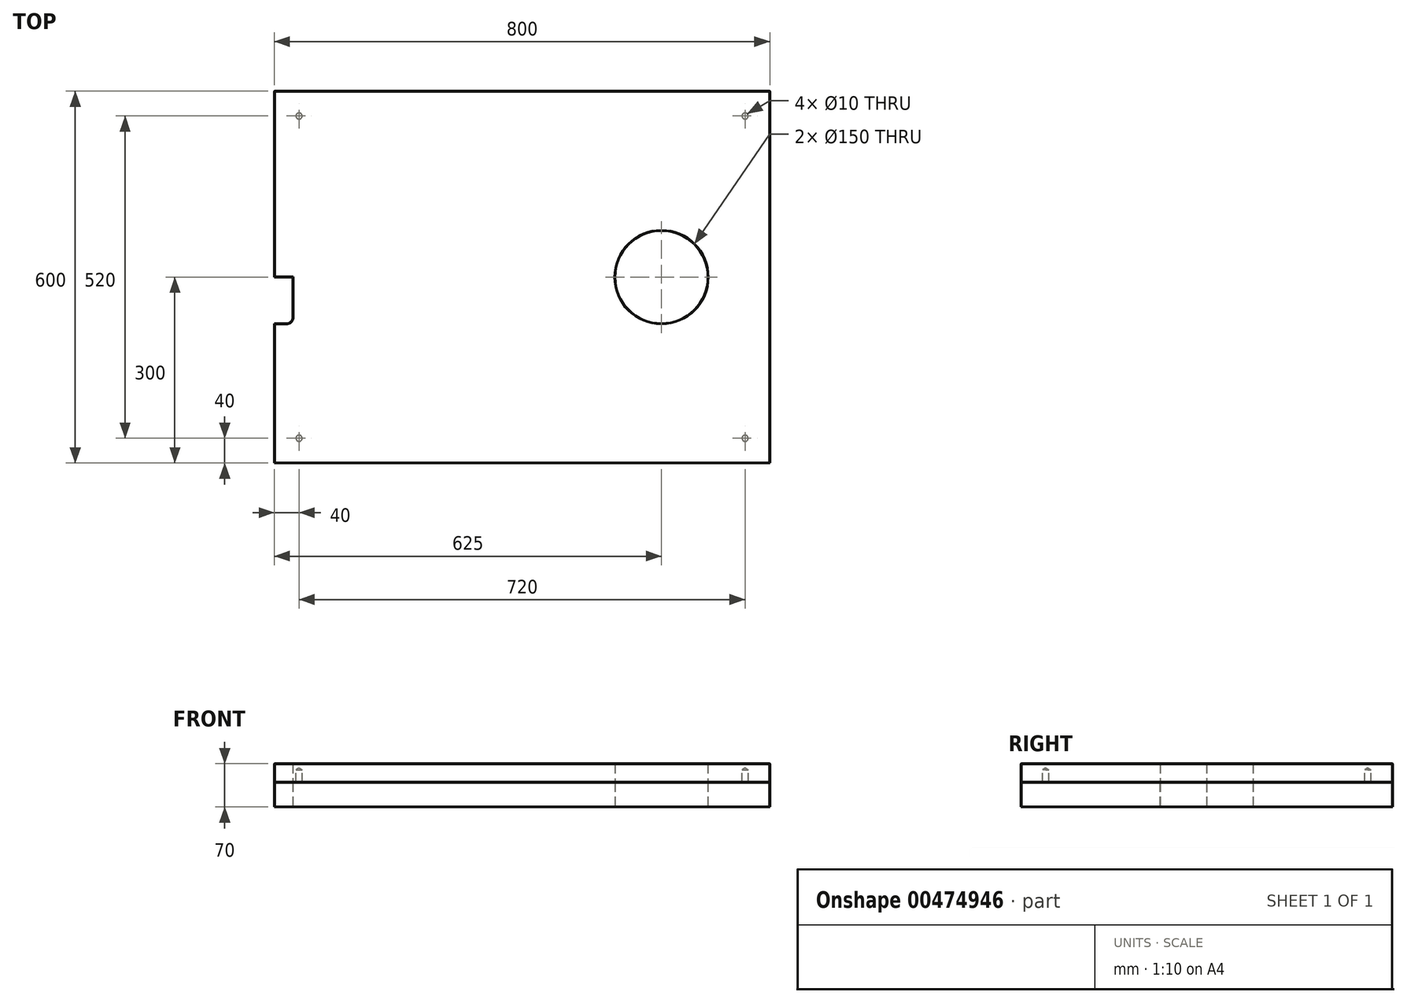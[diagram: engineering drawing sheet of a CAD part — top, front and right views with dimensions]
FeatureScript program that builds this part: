
annotation { "Feature Type Name" : "Feature", "Feature Type Description" : "" }
export const myFeature = defineFeature(function(context is Context, id is Id, definition is map)
    precondition{}
    {
        {
            var Q0;
            Q0=qCreatedBy(makeId("Top.planeOp"),FACE);
            var sketch = newSketch(context, id + "F0", { "sketchPlane" : qUnion([Q0])});
            skLineSegment(sketch, "E0", {"start": v(-450, 0) * mm, "end": v(350, 0) * mm, "construction": true});
            skLineSegment(sketch, "E1.bottom", {"start": v(350, 75) * mm, "end": v(330, 75) * mm});
            skLineSegment(sketch, "E1.top", {"start": v(350, -75) * mm, "end": v(330, -75) * mm});
            skLineSegment(sketch, "E1.left", {"start": v(350, 75) * mm, "end": v(350, -75) * mm});
            skLineSegment(sketch, "E1.right", {"start": v(320, 65) * mm, "end": v(320, -65) * mm});
            skPoint(sketch, "E2.visualSharp", {"position": v(320, -75) * mm});
            skArc(sketch, "E2.filletArc", {"start": v(320, -65) * mm, "mid": v(322.93, -72.07) * mm, "end": v(330, -75) * mm});
            skPoint(sketch, "E3.visualSharp", {"position": v(320, 75) * mm});
            skArc(sketch, "E3.filletArc", {"start": v(330, 75) * mm, "mid": v(322.93, 72.07) * mm, "end": v(320, 65) * mm});
            skLineSegment(sketch, "E4", {"start": v(-50, 300) * mm, "end": v(-50, -300) * mm, "construction": true});
            skLineSegment(sketch, "E5.MirrorCS", {"start": v(-450, 75) * mm, "end": v(-430, 75) * mm});
            skLineSegment(sketch, "E6.MirrorCS", {"start": v(-420, 65) * mm, "end": v(-420, -65) * mm});
            skArc(sketch, "E7.MirrorCS", {"start": v(-420, -65) * mm, "mid": v(-422.93, -72.07) * mm, "end": v(-430, -75) * mm});
            skArc(sketch, "E8.MirrorCS", {"start": v(-430, 75) * mm, "mid": v(-422.93, 72.07) * mm, "end": v(-420, 65) * mm});
            skLineSegment(sketch, "E9.MirrorCS", {"start": v(-450, -75) * mm, "end": v(-430, -75) * mm});
            skPoint(sketch, "E10", {"position": v(-410, 260) * mm});
            skPoint(sketch, "E11", {"position": v(310, 260) * mm});
            skPoint(sketch, "E12", {"position": v(310, -260) * mm});
            skPoint(sketch, "E13", {"position": v(-410, -260) * mm});
            skLineSegment(sketch, "E14", {"start": v(-420, 0) * mm, "end": v(-450, 0) * mm});
            skLineSegment(sketch, "E15.bottom", {"start": v(350, 300) * mm, "end": v(-450, 300) * mm});
            skLineSegment(sketch, "E15.top", {"start": v(350, -300) * mm, "end": v(-450, -300) * mm});
            skLineSegment(sketch, "E15.left", {"start": v(350, 300) * mm, "end": v(350, -300) * mm});
            skLineSegment(sketch, "E15.right", {"start": v(-450, 300) * mm, "end": v(-450, -300) * mm});
            skPoint(sketch, "E15.middle", {"position": v(-50, 0) * mm});
            skPoint(sketch, "E16", {"position": v(175, 0) * mm});
            skCircle(sketch, "E17", {"center": v(175, 0) * mm, "radius": 75 * mm});
            skSolve(sketch);
        }
        {
            var Q0;
            Q0=makeQuery(id+"F0.imprint","IMPRINT",FACE,{"disambiguationData":[TD([[makeQuery(id+"F0.imprint","IMPRINT",EDGE,{"derivedFrom":sQuery(id+"F0.wireOp",EDGE,"9696f999-dd8b-4db2-95aa-c8651f8d9f2f.bottom")}),1.0]])]});
            var Q1;
            {var subQ5=sQuery(id+"F0.wireOp",EDGE,"E1.bottom");Q1=makeQuery(id+"F0.imprint","IMPRINT",FACE,{"disambiguationData":[TD([[makeQuery(id+"F0.imprint","IMPRINT",EDGE,{"derivedFrom":subQ5}),-1.0]])]});}
            var Q2;
            {var subQ1=sQuery(id+"F0.wireOp",EDGE,"E1.bottom");Q2=makeQuery(id+"F0.imprint","IMPRINT",FACE,{"disambiguationData":[TD([[makeQuery(id+"F0.imprint","IMPRINT",EDGE,{"derivedFrom":subQ1}),1.0]])]});}
            var Q3;
            {var subQ2=sQuery(id+"F0.wireOp",EDGE,"E7.MirrorCS");Q3=makeQuery(id+"F0.imprint","IMPRINT",FACE,{"disambiguationData":[TD([[makeQuery(id+"F0.imprint","IMPRINT",EDGE,{"derivedFrom":subQ2}),-1.0]])]});}
            var Q4;
            {var subQ3=sQuery(id+"F0.wireOp",EDGE,"E5.MirrorCS");Q4=makeQuery(id+"F0.imprint","IMPRINT",FACE,{"disambiguationData":[TD([[makeQuery(id+"F0.imprint","IMPRINT",EDGE,{"derivedFrom":subQ3}),-1.0]])]});}
            extrude(context, id + "F1", {"entities" : qUnion([Q0, Q1, Q2, Q3, Q4]), "depth" : 40 * mm, "offsetDistance" : 25 * mm});
        }
        {
            var Q0;
            Q0=makeQuery(id+"F1.opExtrude","CAP_FACE",FACE,{"disambiguationData":[OSD([sQuery(id+"F0.wireOp",EDGE,"E15.bottom"),sQuery(id+"F0.wireOp",EDGE,"E15.top"),sQuery(id+"F0.wireOp",EDGE,"E15.left"),sQuery(id+"F0.wireOp",EDGE,"E15.right")])],"isStart":false});
            var sketch = newSketch(context, id + "F2", { "sketchPlane" : qUnion([Q0])});
            skLineSegment(sketch, "E18.0", {"start": v(350, -75) * mm, "end": v(330, -75) * mm});
            skArc(sketch, "E19.0", {"start": v(320, -65) * mm, "mid": v(322.93, -72.07) * mm, "end": v(330, -75) * mm});
            skLineSegment(sketch, "E20.0", {"start": v(320, 65) * mm, "end": v(320, -65) * mm});
            skArc(sketch, "E21.0", {"start": v(330, 75) * mm, "mid": v(322.93, 72.07) * mm, "end": v(320, 65) * mm});
            skLineSegment(sketch, "E22.0", {"start": v(350, 75) * mm, "end": v(330, 75) * mm});
            skLineSegment(sketch, "E23.0", {"start": v(-450, -75) * mm, "end": v(-430, -75) * mm});
            skArc(sketch, "E24.0", {"start": v(-420, -65) * mm, "mid": v(-422.93, -72.07) * mm, "end": v(-430, -75) * mm});
            skLineSegment(sketch, "E25.0", {"start": v(-420, 65) * mm, "end": v(-420, -65) * mm});
            skArc(sketch, "E26.0", {"start": v(-430, 75) * mm, "mid": v(-422.93, 72.07) * mm, "end": v(-420, 65) * mm});
            skLineSegment(sketch, "E27.0", {"start": v(-450, 75) * mm, "end": v(-430, 75) * mm});
            skSolve(sketch);
        }
        {
            var Q0;
            Q0=makeQuery(id+"F1.opExtrude","CAP_FACE",FACE,{"disambiguationData":[OSD([sQuery(id+"F0.wireOp",EDGE,"E1.bottom"),sQuery(id+"F0.wireOp",EDGE,"E1.top"),sQuery(id+"F0.wireOp",EDGE,"E1.right"),sQuery(id+"F0.wireOp",EDGE,"E2.filletArc"),sQuery(id+"F0.wireOp",EDGE,"E3.filletArc"),sQuery(id+"F0.wireOp",EDGE,"E5.MirrorCS"),sQuery(id+"F0.wireOp",EDGE,"E6.MirrorCS"),sQuery(id+"F0.wireOp",EDGE,"E7.MirrorCS"),sQuery(id+"F0.wireOp",EDGE,"E8.MirrorCS"),sQuery(id+"F0.wireOp",EDGE,"E9.MirrorCS"),sQuery(id+"F0.wireOp",EDGE,"E15.bottom"),sQuery(id+"F0.wireOp",EDGE,"E15.top"),sQuery(id+"F0.wireOp",EDGE,"E15.left"),sQuery(id+"F0.wireOp",EDGE,"E15.right")])],"isStart":false});
            var sketch = newSketch(context, id + "F3", { "sketchPlane" : qUnion([Q0])});
            skLineSegment(sketch, "E28.bottom", {"start": v(-450, 300) * mm, "end": v(350, 300) * mm});
            skLineSegment(sketch, "E28.top", {"start": v(-450, -300) * mm, "end": v(350, -300) * mm});
            skLineSegment(sketch, "E28.left", {"start": v(-450, 300) * mm, "end": v(-450, -300) * mm});
            skLineSegment(sketch, "E28.right", {"start": v(350, 300) * mm, "end": v(350, -300) * mm});
            skLineSegment(sketch, "E29.0", {"start": v(-410, 260) * mm, "end": v(310, 260) * mm});
            skLineSegment(sketch, "E29.1", {"start": v(-410, 260) * mm, "end": v(-410, -260) * mm});
            skLineSegment(sketch, "E29.2", {"start": v(-410, -260) * mm, "end": v(310, -260) * mm});
            skLineSegment(sketch, "E29.3", {"start": v(310, 260) * mm, "end": v(310, -260) * mm});
            skSolve(sketch);
        }
        {
            var Q0;
            {var subQ1=makeQuery(id+"F1.opExtrude","CAP_EDGE",EDGE,{"disambiguationData":[OSD([sQuery(id+"F0.wireOp",EDGE,"E1.bottom")])],"isStart":false});Q0=makeQuery(id+"F3.imprint","IMPRINT",FACE,{"disambiguationData":[TD([[makeQuery(id+"F3.imprint","IMPRINT",EDGE,{"derivedFrom":subQ1}),1.0]])]});}
            var Q1;
            {var subQ4=sQuery(id+"F3.wireOp",EDGE,"E28.bottom");Q1=makeQuery(id+"F3.imprint","IMPRINT",FACE,{"disambiguationData":[TD([[makeQuery(id+"F3.imprint","IMPRINT",EDGE,{"derivedFrom":subQ4}),1.0]])]});}
            var Q2;
            {var subQ0=makeQuery(id+"F1.opExtrude","CAP_EDGE",EDGE,{"disambiguationData":[OSD([sQuery(id+"F0.wireOp",EDGE,"E5.MirrorCS")])],"isStart":false});Q2=makeQuery(id+"F3.imprint","IMPRINT",FACE,{"disambiguationData":[TD([[makeQuery(id+"F3.imprint","IMPRINT",EDGE,{"derivedFrom":subQ0}),-1.0]])]});}
            var Q3;
            Q3=makeQuery(id+"F3.imprint","IMPRINT",FACE,{"disambiguationData":[TD([[makeQuery(id+"F3.imprint","IMPRINT",EDGE,{"derivedFrom":sQuery(id+"F3.wireOp",EDGE,"E29.0")}),-1.0]])]});
            var Q4;
            {var subQ4=sQuery(id+"F3.wireOp",EDGE,"E28.bottom");Q4=makeQuery(id+"F3.imprint","IMPRINT",FACE,{"disambiguationData":[TD([[makeQuery(id+"F3.imprint","IMPRINT",EDGE,{"derivedFrom":subQ4}),1.0]])]});}
            var Q5;
            Q5=makeQuery(id+"F3.imprint","IMPRINT",FACE,{"disambiguationData":[TD([[makeQuery(id+"F3.imprint","IMPRINT",EDGE,{"derivedFrom":sQuery(id+"F3.wireOp",EDGE,"E29.0")}),-1.0]])]});
            var Q6;
            {var subQ0=makeQuery(id+"FIPpv0qjfYkindW_1.boolean.opBoolean","COPY",EDGE,{"derivedFrom":makeQuery(id+"FIPpv0qjfYkindW_1.opExtrude","CAP_EDGE",EDGE,{"disambiguationData":[OSD([sQuery(id+"F2.wireOp",EDGE,"E18.0")])],"isStart":true})});Q6=makeQuery(id+"F3.imprint","IMPRINT",FACE,{"disambiguationData":[TD([[makeQuery(id+"F3.imprint","IMPRINT",EDGE,{"derivedFrom":subQ0}),-1.0]])]});}
            var Q7;
            {var subQ0=makeQuery(id+"FIPpv0qjfYkindW_1.boolean.opBoolean","COPY",EDGE,{"derivedFrom":makeQuery(id+"FIPpv0qjfYkindW_1.opExtrude","CAP_EDGE",EDGE,{"disambiguationData":[OSD([sQuery(id+"F2.wireOp",EDGE,"E23.0")])],"isStart":true})});Q7=makeQuery(id+"F3.imprint","IMPRINT",FACE,{"disambiguationData":[TD([[makeQuery(id+"F3.imprint","IMPRINT",EDGE,{"derivedFrom":subQ0}),1.0]])]});}
            extrude(context, id + "F4", {"entities" : qUnion([Q0, Q1, Q2, Q3, Q4, Q5, Q6, Q7]), "depth" : 30 * mm});
        }
        {
            var Q0;
            Q0=makeQuery(id+"F4.opExtrude","CAP_FACE",FACE,{"disambiguationData":[OSD([sQuery(id+"F3.wireOp",EDGE,"E28.bottom"),sQuery(id+"F3.wireOp",EDGE,"E28.top"),sQuery(id+"F3.wireOp",EDGE,"E28.left"),sQuery(id+"F3.wireOp",EDGE,"E28.right")])],"isStart":false});
            var Q1;
            Q1=makeQuery(id+"F4.opExtrude","CAP_FACE",FACE,{"disambiguationData":[OSD([sQuery(id+"F3.wireOp",EDGE,"E28.bottom"),sQuery(id+"F3.wireOp",EDGE,"E28.top"),sQuery(id+"F3.wireOp",EDGE,"E28.left"),sQuery(id+"F3.wireOp",EDGE,"E28.right")])],"isStart":true});
            var Q2;
            Q2=makeQuery(id+"F4.opExtrude","SWEPT_EDGE",EDGE,{"disambiguationData":[OSD([sQuery(id+"F3.wireOp",EDGE,"E28.bottom"),sQuery(id+"F3.wireOp",EDGE,"E28.right")])]});
            var Q3;
            Q3=makeQuery(id+"F4.opExtrude","SWEPT_EDGE",EDGE,{"disambiguationData":[OSD([sQuery(id+"F3.wireOp",EDGE,"E28.bottom"),sQuery(id+"F3.wireOp",EDGE,"E28.left")])]});
            var Q4;
            Q4=makeQuery(id+"F4.opExtrude","SWEPT_EDGE",EDGE,{"disambiguationData":[OSD([sQuery(id+"F3.wireOp",EDGE,"E28.top"),sQuery(id+"F3.wireOp",EDGE,"E28.left")])]});
            var Q5;
            Q5=makeQuery(id+"F4.opExtrude","SWEPT_EDGE",EDGE,{"disambiguationData":[OSD([sQuery(id+"F3.wireOp",EDGE,"E28.top"),sQuery(id+"F3.wireOp",EDGE,"E28.right")])]});
            chamfer(context, id + "F5", {"entities" : qUnion([Q0, Q1, Q2, Q3, Q4, Q5]), "width" : 0.5 * mm, "tangentPropagation" : true});
        }
        {
            var Q0;
            Q0=sQuery(id+"F3.wireOp",VERTEX,"E29.1.start");
            var Q1;
            Q1=sQuery(id+"F3.wireOp",VERTEX,"E29.0.end");
            var Q2;
            Q2=sQuery(id+"F3.wireOp",VERTEX,"E29.3.end");
            var Q3;
            Q3=sQuery(id+"F3.wireOp",VERTEX,"E29.2.start");
            var Q4;
            Q4=makeQuery(id+"F4.opExtrude","SWEPT_BODY",BODY,{"disambiguationData":[OSD([sQuery(id+"F3.wireOp",EDGE,"E28.bottom"),sQuery(id+"F3.wireOp",EDGE,"E28.top"),sQuery(id+"F3.wireOp",EDGE,"E28.left"),sQuery(id+"F3.wireOp",EDGE,"E28.right")])]});
            hole(context, id + "F6", {"style" : HoleStyle.SIMPLE, "endStyle" : HoleEndStyle.BLIND, "oppositeDirection" : true, "holeDiameter" : 10 * mm, "holeDepth" : 20 * mm, "isTappedThrough" : true, "tappedDepth" : 12 * mm, "tapClearance" : 3, "locations" : qUnion([Q0, Q1, Q2, Q3]), "scope" : qUnion([Q4]), "startStyle" : HoleStartStyle.PART});
        }
        {
            var Q0;
            Q0=makeQuery(id+"F1.opExtrude","CAP_FACE",FACE,{"disambiguationData":[OSD([sQuery(id+"F0.wireOp",EDGE,"E1.bottom"),sQuery(id+"F0.wireOp",EDGE,"E1.top"),sQuery(id+"F0.wireOp",EDGE,"E1.right"),sQuery(id+"F0.wireOp",EDGE,"E2.filletArc"),sQuery(id+"F0.wireOp",EDGE,"E3.filletArc"),sQuery(id+"F0.wireOp",EDGE,"E5.MirrorCS"),sQuery(id+"F0.wireOp",EDGE,"E6.MirrorCS"),sQuery(id+"F0.wireOp",EDGE,"E7.MirrorCS"),sQuery(id+"F0.wireOp",EDGE,"E8.MirrorCS"),sQuery(id+"F0.wireOp",EDGE,"E9.MirrorCS"),sQuery(id+"F0.wireOp",EDGE,"E15.bottom"),sQuery(id+"F0.wireOp",EDGE,"E15.top"),sQuery(id+"F0.wireOp",EDGE,"E15.left"),sQuery(id+"F0.wireOp",EDGE,"E15.right")])],"isStart":false});
            var Q1;
            {var subQ0=sQuery(id+"F0.wireOp",EDGE,"E15.right");var subQ1=sQuery(id+"F0.wireOp",EDGE,"E15.left");var subQ2=sQuery(id+"F0.wireOp",EDGE,"E15.top");var subQ3=sQuery(id+"F0.wireOp",EDGE,"E15.bottom");Q1=makeQuery(id+"FSn3DBmeKnvXifK_2.boolean.opBoolean","MERGE",FACE,{"derivedFrom":[makeQuery(id+"F1.opExtrude","CAP_FACE",FACE,{"disambiguationData":[OSD([sQuery(id+"F0.wireOp",EDGE,"E1.bottom"),sQuery(id+"F0.wireOp",EDGE,"E1.top"),sQuery(id+"F0.wireOp",EDGE,"E1.right"),sQuery(id+"F0.wireOp",EDGE,"E2.filletArc"),sQuery(id+"F0.wireOp",EDGE,"E3.filletArc"),sQuery(id+"F0.wireOp",EDGE,"E5.MirrorCS"),sQuery(id+"F0.wireOp",EDGE,"E6.MirrorCS"),sQuery(id+"F0.wireOp",EDGE,"E7.MirrorCS"),sQuery(id+"F0.wireOp",EDGE,"E8.MirrorCS"),sQuery(id+"F0.wireOp",EDGE,"E9.MirrorCS"),subQ3,subQ2,subQ1,subQ0])],"isStart":true}),makeQuery(id+"FSn3DBmeKnvXifK_2.opExtrude","CAP_FACE",FACE,{"disambiguationData":[OSD([subQ3,subQ2,subQ1,subQ0])],"isStart":true})]});}
            var Q2;
            Q2=makeQuery(id+"F1.opExtrude","SWEPT_FACE",FACE,{"disambiguationData":[OSD([sQuery(id+"F0.wireOp",EDGE,"E15.top")])]});
            var Q3;
            {var subQ0=sQuery(id+"F0.wireOp",EDGE,"E15.left");Q3=makeQuery(id+"FSn3DBmeKnvXifK_2.boolean.opBoolean","MERGE",FACE,{"derivedFrom":[makeQuery(id+"F1.opExtrude","SWEPT_FACE",FACE,{"disambiguationData":[OSD([subQ0]),TDD([makeQuery(id+"F0.imprint","IMPRINT",EDGE,{"disambiguationData":[TD([[makeQuery(id+"F0.imprint","INTERSECT",VERTEX,{"derivedFrom":[sQuery(id+"F0.wireOp",EDGE,"E1.bottom"),subQ0]}),1.0]])],"derivedFrom":subQ0})])]}),makeQuery(id+"F1.opExtrude","SWEPT_FACE",FACE,{"disambiguationData":[OSD([subQ0]),TDD([makeQuery(id+"F0.imprint","IMPRINT",EDGE,{"disambiguationData":[TD([[makeQuery(id+"F0.imprint","INTERSECT",VERTEX,{"derivedFrom":[sQuery(id+"F0.wireOp",EDGE,"E1.top"),subQ0]}),-1.0]])],"derivedFrom":subQ0})])]}),makeQuery(id+"FSn3DBmeKnvXifK_2.opExtrude","SWEPT_FACE",FACE,{"disambiguationData":[OSD([subQ0])]})]});}
            var Q4;
            {var subQ0=sQuery(id+"F0.wireOp",EDGE,"E15.right");Q4=makeQuery(id+"FSn3DBmeKnvXifK_2.boolean.opBoolean","MERGE",FACE,{"derivedFrom":[makeQuery(id+"F1.opExtrude","SWEPT_FACE",FACE,{"disambiguationData":[OSD([subQ0]),TDD([makeQuery(id+"F0.imprint","IMPRINT",EDGE,{"disambiguationData":[TD([[makeQuery(id+"F0.imprint","INTERSECT",VERTEX,{"derivedFrom":[sQuery(id+"F0.wireOp",EDGE,"E5.MirrorCS"),subQ0]}),1.0]])],"derivedFrom":subQ0})])]}),makeQuery(id+"F1.opExtrude","SWEPT_FACE",FACE,{"disambiguationData":[OSD([subQ0]),TDD([makeQuery(id+"F0.imprint","IMPRINT",EDGE,{"disambiguationData":[TD([[makeQuery(id+"F0.imprint","INTERSECT",VERTEX,{"derivedFrom":[sQuery(id+"F0.wireOp",EDGE,"E9.MirrorCS"),subQ0]}),-1.0]])],"derivedFrom":subQ0})])]}),makeQuery(id+"FSn3DBmeKnvXifK_2.opExtrude","SWEPT_FACE",FACE,{"disambiguationData":[OSD([subQ0])]})]});}
            var Q5;
            Q5=makeQuery(id+"F1.opExtrude","SWEPT_FACE",FACE,{"disambiguationData":[OSD([sQuery(id+"F0.wireOp",EDGE,"E15.bottom")])]});
            var Q6;
            {var subQ0=sQuery(id+"F0.wireOp",EDGE,"E17");Q6=makeQuery(id+"F5.opChamfer","BLEND_EDGE",EDGE,{"blendedFrom":[makeQuery(id+"F4.opExtrude","CAP_EDGE",EDGE,{"disambiguationData":[OSD([subQ0])],"isStart":false}),makeQuery(id+"F4.opExtrude","SWEPT_FACE",FACE,{"disambiguationData":[OSD([subQ0])]})],"blendedInto":[makeQuery(id+"F4.opExtrude","SWEPT_FACE",FACE,{"disambiguationData":[OSD([subQ0])]})]});}
            chamfer(context, id + "F7", {"entities" : qUnion([Q0, Q1, Q2, Q3, Q4, Q5, Q6]), "width" : 0.5 * mm, "tangentPropagation" : true});
        }
    });
